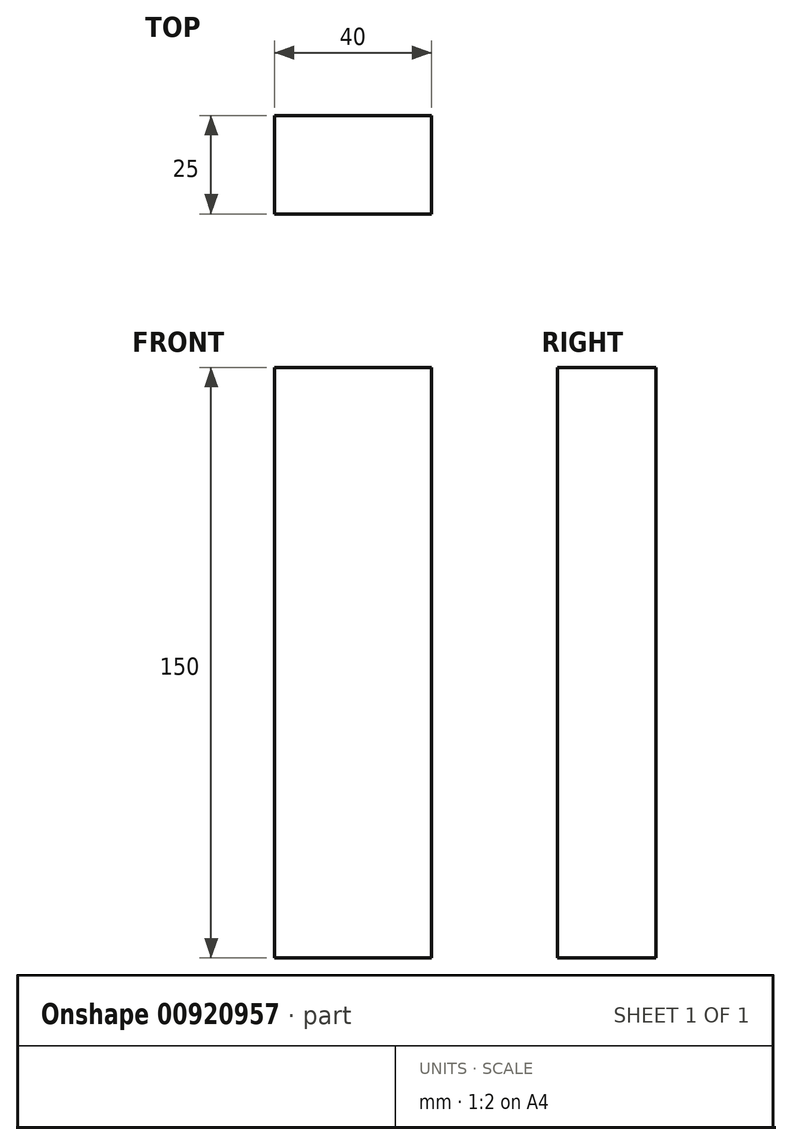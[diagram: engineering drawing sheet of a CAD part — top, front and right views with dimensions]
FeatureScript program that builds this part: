
annotation { "Feature Type Name" : "Feature", "Feature Type Description" : "" }
export const myFeature = defineFeature(function(context is Context, id is Id, definition is map)
    precondition{}
    {
        {
            var Q0;
            Q0=qCreatedBy(makeId("Front.planeOp"),FACE);
            var sketch = newSketch(context, id + "F0", { "sketchPlane" : qUnion([Q0])});
            skLineSegment(sketch, "E0.bottom", {"start": v(20, -75) * mm, "end": v(-20, -75) * mm});
            skLineSegment(sketch, "E0.top", {"start": v(20, 75) * mm, "end": v(-20, 75) * mm});
            skLineSegment(sketch, "E0.left", {"start": v(20, -75) * mm, "end": v(20, 75) * mm});
            skLineSegment(sketch, "E0.right", {"start": v(-20, -75) * mm, "end": v(-20, 75) * mm});
            skPoint(sketch, "E0.middle", {"position": v(0, 0) * mm});
            skSolve(sketch);
        }
        {
            var Q0;
            Q0 = qSketchRegion(id + "F0", true);
            extrude(context, id + "F1", {"entities" : qUnion([Q0]), "depth" : 25 * mm, "offsetDistance" : 25 * mm});
        }
    });
